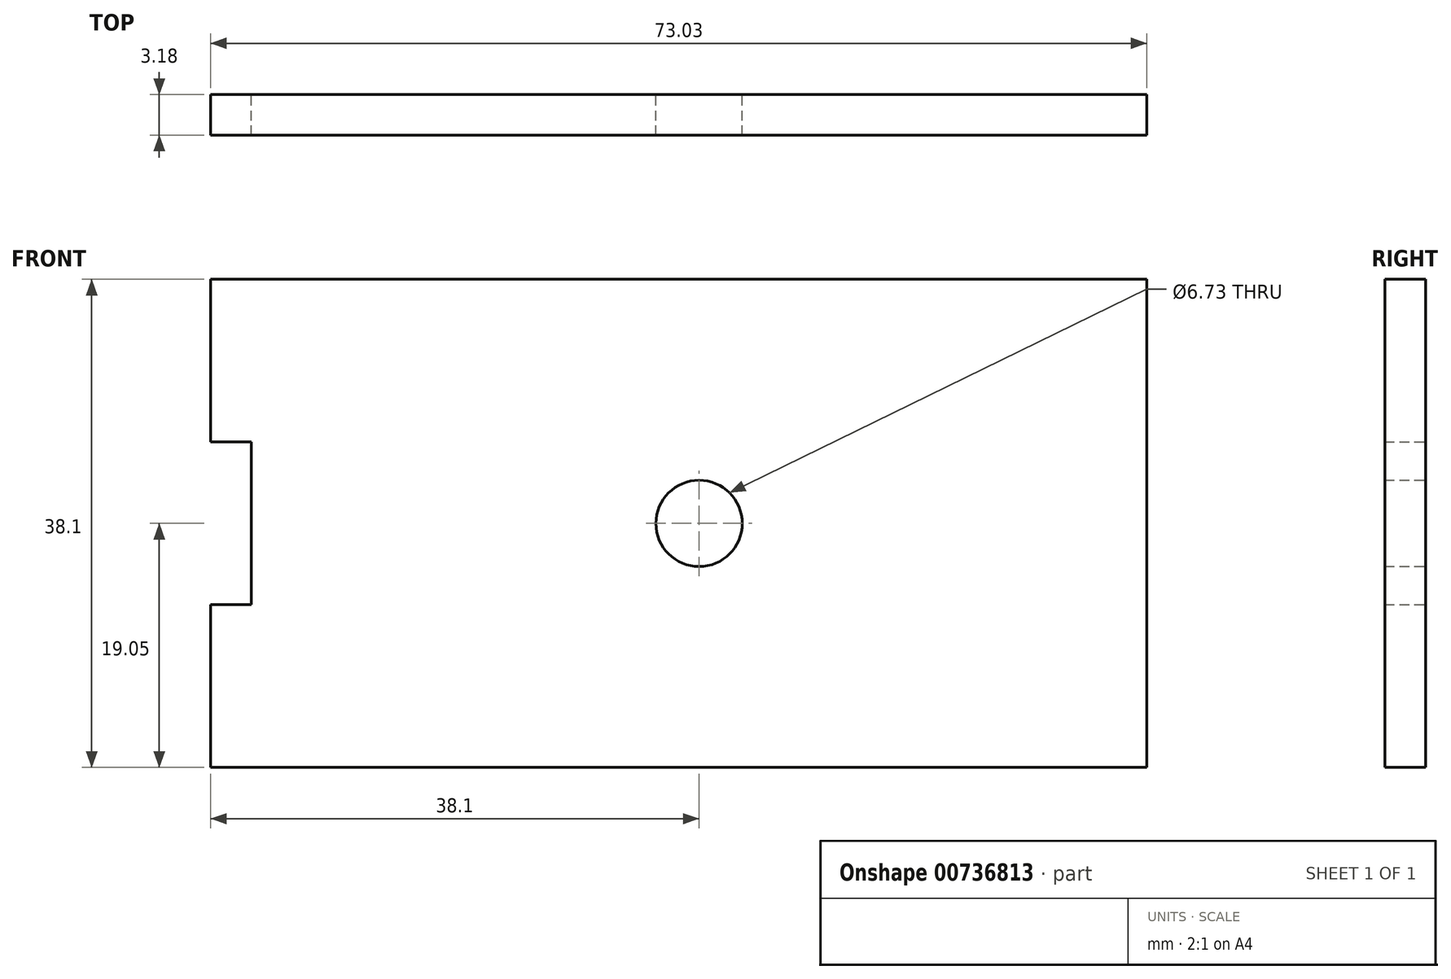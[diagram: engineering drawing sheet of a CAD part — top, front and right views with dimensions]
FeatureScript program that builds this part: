
annotation { "Feature Type Name" : "Feature", "Feature Type Description" : "" }
export const myFeature = defineFeature(function(context is Context, id is Id, definition is map)
    precondition{}
    {
        {
            var Q0;
            Q0=qCreatedBy(makeId("Front.planeOp"),FACE);
            var sketch = newSketch(context, id + "F0", { "sketchPlane" : qUnion([Q0])});
            skLineSegment(sketch, "E0.bottom", {"start": v(0, 0) * mm, "end": v(-76.2, 0) * mm});
            skLineSegment(sketch, "E0.top", {"start": v(0, 38.1) * mm, "end": v(-76.2, 38.1) * mm});
            skLineSegment(sketch, "E0.left", {"start": v(0, 0) * mm, "end": v(0, 38.1) * mm});
            skLineSegment(sketch, "E0.right", {"start": v(-76.2, 0) * mm, "end": v(-76.2, 38.1) * mm});
            skLineSegment(sketch, "E1", {"start": v(-38.1, 0) * mm, "end": v(-38.1, 38.1) * mm});
            skCircle(sketch, "E2", {"center": v(-38.1, 19.05) * mm, "radius": 3.37 * mm});
            skLineSegment(sketch, "E3.bottom", {"start": v(0, 0) * mm, "end": v(-3.17, 0) * mm});
            skLineSegment(sketch, "E3.top", {"start": v(0, 12.7) * mm, "end": v(-3.18, 12.7) * mm});
            skLineSegment(sketch, "E3.left", {"start": v(0, 0) * mm, "end": v(0, 12.7) * mm});
            skLineSegment(sketch, "E3.right", {"start": v(-3.17, 0) * mm, "end": v(-3.18, 12.7) * mm});
            skLineSegment(sketch, "E4.bottom", {"start": v(0, 38.1) * mm, "end": v(-3.18, 38.1) * mm});
            skLineSegment(sketch, "E4.top", {"start": v(0, 25.4) * mm, "end": v(-3.18, 25.4) * mm});
            skLineSegment(sketch, "E4.left", {"start": v(0, 38.1) * mm, "end": v(0, 25.4) * mm});
            skLineSegment(sketch, "E4.right", {"start": v(-3.18, 38.1) * mm, "end": v(-3.18, 25.4) * mm});
            skLineSegment(sketch, "E5.MirrorCS", {"start": v(-73.02, 38.1) * mm, "end": v(-73.02, 25.4) * mm});
            skLineSegment(sketch, "E6.MirrorCS", {"start": v(-76.2, 25.4) * mm, "end": v(-73.02, 25.4) * mm});
            skLineSegment(sketch, "E7.MirrorCS", {"start": v(-76.2, 12.7) * mm, "end": v(-73.03, 12.7) * mm});
            skLineSegment(sketch, "E8.MirrorCS", {"start": v(-73.03, 0) * mm, "end": v(-73.03, 12.7) * mm});
            skLineSegment(sketch, "E9", {"start": v(-3.18, 12.7) * mm, "end": v(-3.18, 25.4) * mm});
            skLineSegment(sketch, "E10.MirrorCS", {"start": v(-73.03, 12.7) * mm, "end": v(-73.03, 25.4) * mm});
            skSolve(sketch);
        }
        {
            var Q0;
            {var subQ4=sQuery(id+"F0.wireOp",EDGE,"E7.MirrorCS");Q0=makeQuery(id+"F0.imprint","IMPRINT",FACE,{"disambiguationData":[TD([[makeQuery(id+"F0.imprint","IMPRINT",EDGE,{"derivedFrom":subQ4}),-1.0]])]});}
            var Q1;
            {var subQ8=sQuery(id+"F0.wireOp",EDGE,"E5.MirrorCS");Q1=makeQuery(id+"F0.imprint","IMPRINT",FACE,{"disambiguationData":[TD([[makeQuery(id+"F0.imprint","IMPRINT",EDGE,{"derivedFrom":subQ8}),1.0]])]});}
            var Q2;
            {var subQ3=sQuery(id+"F0.wireOp",EDGE,"E5.MirrorCS");Q2=makeQuery(id+"F0.imprint","IMPRINT",FACE,{"disambiguationData":[TD([[makeQuery(id+"F0.imprint","IMPRINT",EDGE,{"derivedFrom":subQ3}),-1.0]])]});}
            var Q3;
            {var subQ9=sQuery(id+"F0.wireOp",EDGE,"E3.right");Q3=makeQuery(id+"F0.imprint","IMPRINT",FACE,{"disambiguationData":[TD([[makeQuery(id+"F0.imprint","IMPRINT",EDGE,{"derivedFrom":subQ9}),1.0]])]});}
            var Q4;
            Q4=makeQuery(id+"F0.imprint","IMPRINT",FACE,{"disambiguationData":[TD([[makeQuery(id+"F0.imprint","IMPRINT",EDGE,{"derivedFrom":sQuery(id+"F0.wireOp",EDGE,"E3.bottom")}),-1.0]])]});
            var Q5;
            Q5=makeQuery(id+"F0.imprint","IMPRINT",FACE,{"disambiguationData":[TD([[makeQuery(id+"F0.imprint","IMPRINT",EDGE,{"derivedFrom":sQuery(id+"F0.wireOp",EDGE,"E4.bottom")}),1.0]])]});
            extrude(context, id + "F1", {"entities" : qUnion([Q0, Q1, Q2, Q3, Q4, Q5]), "depth" : 3.17 * mm, "offsetDistance" : 25.4 * mm});
        }
    });
